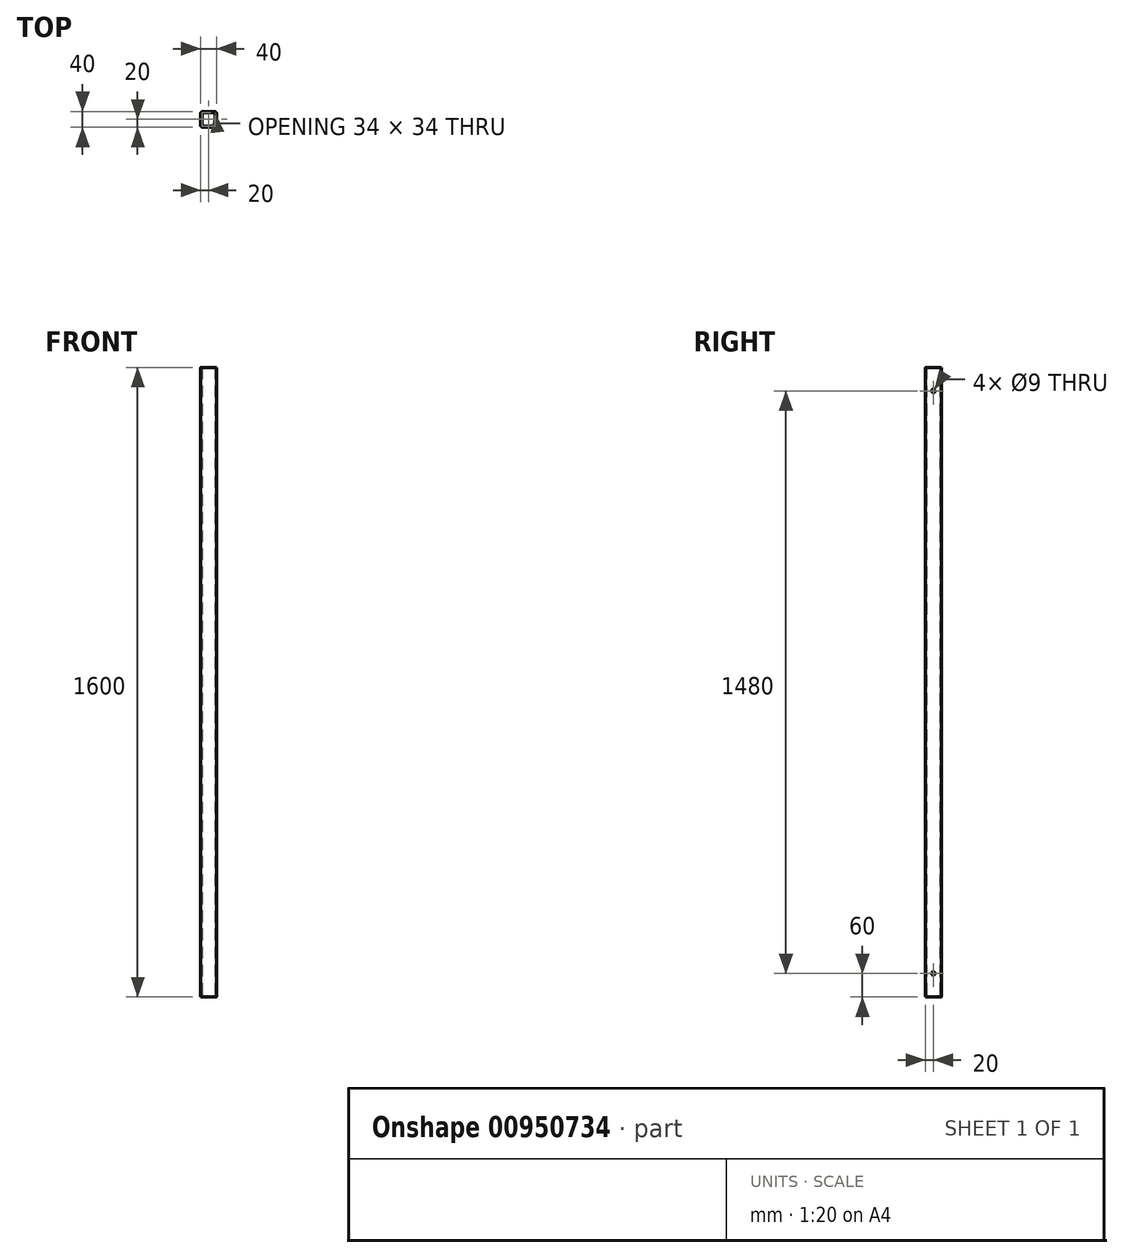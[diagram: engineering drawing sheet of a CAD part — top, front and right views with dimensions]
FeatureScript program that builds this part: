
annotation { "Feature Type Name" : "Feature", "Feature Type Description" : "" }
export const myFeature = defineFeature(function(context is Context, id is Id, definition is map)
    precondition{}
    {
        {
            var Q0;
            Q0=qCreatedBy(makeId("Top.planeOp"),FACE);
            var sketch = newSketch(context, id + "F0", { "sketchPlane" : qUnion([Q0])});
            skLineSegment(sketch, "E0.bottom", {"start": v(15.5, -20) * mm, "end": v(-15.5, -20) * mm});
            skLineSegment(sketch, "E0.top", {"start": v(15.5, 20) * mm, "end": v(-15.5, 20) * mm});
            skLineSegment(sketch, "E0.left", {"start": v(20, -15.5) * mm, "end": v(20, 15.5) * mm});
            skLineSegment(sketch, "E0.right", {"start": v(-20, -15.5) * mm, "end": v(-20, 15.5) * mm});
            skPoint(sketch, "E0.middle", {"position": v(0, 0) * mm});
            skPoint(sketch, "E1.visualSharp", {"position": v(-20, 20) * mm});
            skArc(sketch, "E2.filletArc", {"start": v(-15.5, 20) * mm, "mid": v(-18.68, 18.68) * mm, "end": v(-20, 15.5) * mm});
            skPoint(sketch, "E3.visualSharp", {"position": v(20, 20) * mm});
            skArc(sketch, "E3.filletArc", {"start": v(20, 15.5) * mm, "mid": v(18.68, 18.68) * mm, "end": v(15.5, 20) * mm});
            skPoint(sketch, "E4.visualSharp", {"position": v(20, -20) * mm});
            skArc(sketch, "E4.filletArc", {"start": v(15.5, -20) * mm, "mid": v(18.68, -18.68) * mm, "end": v(20, -15.5) * mm});
            skPoint(sketch, "E5.visualSharp", {"position": v(-20, -20) * mm});
            skArc(sketch, "E5.filletArc", {"start": v(-20, -15.5) * mm, "mid": v(-18.68, -18.68) * mm, "end": v(-15.5, -20) * mm});
            skArc(sketch, "E6.0", {"start": v(17, 15.5) * mm, "mid": v(16.56, 16.56) * mm, "end": v(15.5, 17) * mm});
            skLineSegment(sketch, "E6.1", {"start": v(17, -15.5) * mm, "end": v(17, 15.5) * mm});
            skLineSegment(sketch, "E6.2", {"start": v(15.5, 17) * mm, "end": v(-15.5, 17) * mm});
            skArc(sketch, "E6.3", {"start": v(15.5, -17) * mm, "mid": v(16.56, -16.56) * mm, "end": v(17, -15.5) * mm});
            skArc(sketch, "E6.4", {"start": v(-15.5, 17) * mm, "mid": v(-16.56, 16.56) * mm, "end": v(-17, 15.5) * mm});
            skLineSegment(sketch, "E6.5", {"start": v(-17, -15.5) * mm, "end": v(-17, 15.5) * mm});
            skArc(sketch, "E6.6", {"start": v(-17, -15.5) * mm, "mid": v(-16.56, -16.56) * mm, "end": v(-15.5, -17) * mm});
            skLineSegment(sketch, "E6.7", {"start": v(15.5, -17) * mm, "end": v(-15.5, -17) * mm});
            skSolve(sketch);
        }
        {
            var Q0;
            Q0=qSketchRegion(id+"F0",true);
            extrude(context, id + "F1", {"entities" : qUnion([Q0]), "depth" : 1600 * mm, "offsetDistance" : 25 * mm});
        }
        {
            var Q0;
            Q0=makeQuery(id+"F1.opExtrude","SWEPT_FACE",FACE,{"disambiguationData":[OSD([sQuery(id+"F0.wireOp",EDGE,"E0.left")])]});
            var sketch = newSketch(context, id + "F2", { "sketchPlane" : qUnion([Q0])});
            skLineSegment(sketch, "E7", {"start": v(0, 0) * mm, "end": v(0, 1600) * mm, "construction": true});
            skCircle(sketch, "E8", {"center": v(0, 1540) * mm, "radius": 4.5 * mm});
            skCircle(sketch, "E9", {"center": v(0, 60) * mm, "radius": 4.5 * mm});
            skSolve(sketch);
        }
        {
            var Q0;
            Q0=qSketchRegion(id+"F2",true);
            extrude(context, id + "F3", {"entities" : qUnion([Q0]), "operationType" : NewBodyOperationType.REMOVE, "endBound" : BoundingType.THROUGH_ALL, "oppositeDirection" : true, "depth" : 25 * mm, "offsetDistance" : 25 * mm});
        }
    });
